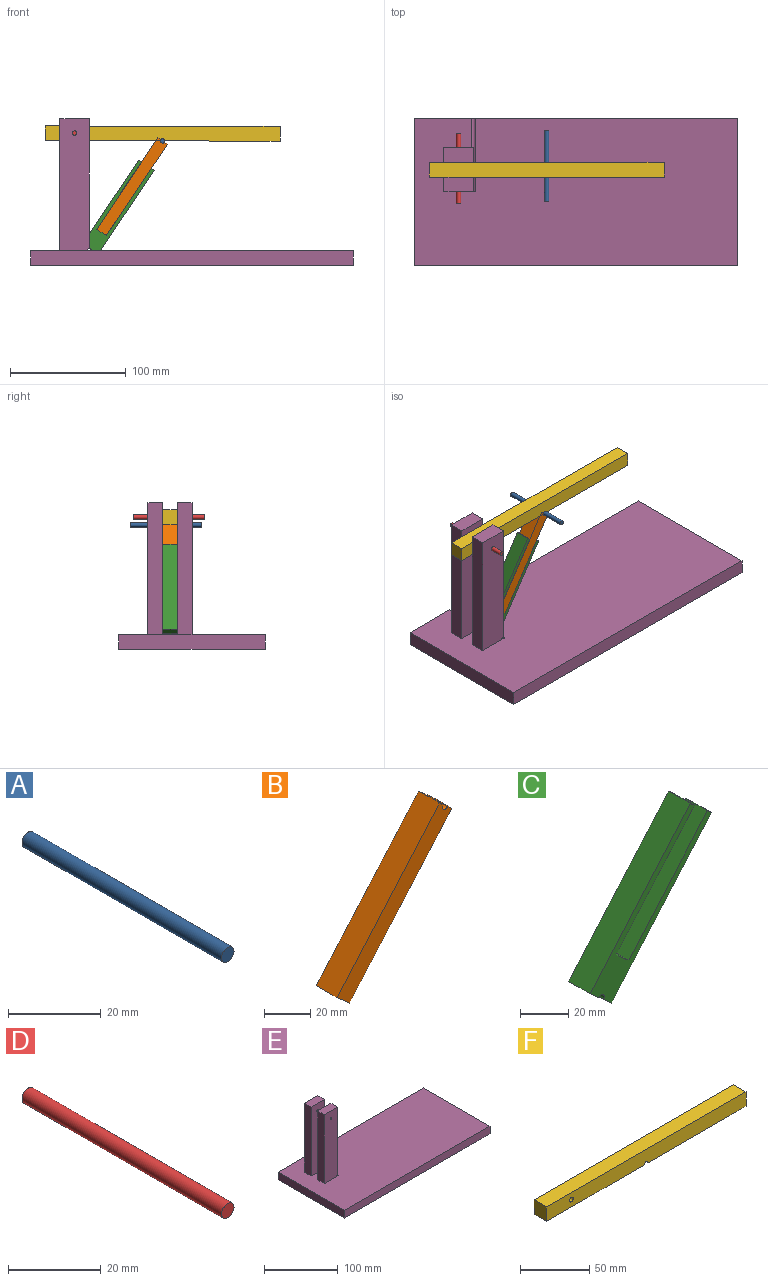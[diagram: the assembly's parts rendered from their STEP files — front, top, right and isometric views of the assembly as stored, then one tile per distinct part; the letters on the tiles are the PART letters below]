
ASSEMBLY  parts=6 mates=10
PART A: 3 faces, bbox 3.8x61x3.8 mm
  f0: cylinder r=1.91mm len=60.96mm, axis (0,1,0), area 729.7mm2, adj f1,f2
  f1: plane 3.81x3.81mm, normal (0,-1,0), area 11.4mm2, adj f0
  f2: plane 3.81x3.81mm, normal (0,1,0), area 11.4mm2, adj f0
PART B: 8 faces, bbox 70x12.7x78.4 mm
  f0: plane 12.7x2.32mm, normal (0.66,0,0.75), area 39.1mm2, adj f1,f5,f6,f7
  f1: plane 71.87x62.51mm, normal (0.75,0,-0.66), area 1209.7mm2, adj f0,f2,f5,f6
  f2: plane 12.7x7.52mm, normal (-0.66,0,-0.75), area 126.5mm2, adj f1,f3,f5,f6
  f3: plane 71.87x62.51mm, normal (-0.75,0,0.66), area 1209.7mm2, adj f2,f4,f5,f6
  f4: plane 12.7x2.32mm, normal (0.66,0,0.75), area 39.1mm2, adj f3,f5,f6,f7
  f5: plane 78.41x70.03mm, normal (0,-1,0), area 943.1mm2, adj f0,f1,f2,f3,f4,f7
  f6: plane 78.41x70.03mm, normal (0,1,0), area 943.1mm2, adj f0,f1,f2,f3,f4,f7
  f7: cylinder r=1.91mm len=12.7mm, axis (0,-1,0), area 76mm2, adj f0,f4,f5,f6
PART C: 12 faces, bbox 70.7x12.7x77.8 mm
  f0: plane 12.7x4.73mm, normal (-0.66,0,-0.75), area 79.6mm2, adj f1,f6,f7,f11
  f1: plane 77.81x70.68mm, normal (0,-1,0), area 752.1mm2, adj f0,f2,f3,f4,f5,f6,f8,f9
  f2: plane 52.7x45.84mm, normal (-0.75,0,0.66), area 887.1mm2, adj f1,f3,f7,f8
  f3: plane 12.7x2.41mm, normal (0.66,0,0.75), area 40.6mm2, adj f1,f2,f4,f7
  f4: plane 67.08x58.34mm, normal (0.75,0,-0.66), area 1129mm2, adj f1,f3,f5,f7
  f5: plane 12.7x4.73mm, normal (-0.66,0,-0.75), area 79.6mm2, adj f1,f4,f7,f11
  f6: plane 67.08x58.34mm, normal (-0.75,0,0.66), area 1129mm2, adj f0,f1,f7,f9
  f7: plane 77.81x70.68mm, normal (0,1,0), area 752.1mm2, adj f0,f2,f3,f4,f5,f6,f8,f9
  f8: plane 12.7x7.52mm, normal (0.66,0,0.75), area 126.5mm2, adj f1,f2,f7,f10
  f9: plane 12.7x2.41mm, normal (0.66,0,0.75), area 40.6mm2, adj f1,f6,f7,f10
  f10: plane 52.7x45.84mm, normal (0.75,0,-0.66), area 887.1mm2, adj f1,f7,f8,f9
  f11: cylinder r=1.91mm len=12.7mm, axis (0,-1,0), area 76mm2, adj f0,f1,f5,f7
PART D: 3 faces, bbox 3.8x61x3.8 mm
  f0: cylinder r=1.91mm len=60.96mm, axis (0,1,0), area 729.7mm2, adj f1,f2
  f1: plane 3.81x3.81mm, normal (0,-1,0), area 11.4mm2, adj f0
  f2: plane 3.81x3.81mm, normal (0,1,0), area 11.4mm2, adj f0
PART E: 20 faces, bbox 279.4x127x127 mm
  f0: plane 279.4x127mm, normal (0,0,1), area 34645.1mm2, adj f1,f2,f3,f4,f6,f8,f9,f12
  f1: plane 127x12.7mm, normal (-1,0,0), area 1612.9mm2, adj f0,f2,f4,f5
  f2: plane 279.4x12.7mm, normal (0,-1,0), area 3548.4mm2, adj f0,f1,f3,f5
  f3: plane 127x12.7mm, normal (1,0,0), area 1612.9mm2, adj f0,f2,f4,f5
  f4: plane 279.4x12.7mm, normal (0,1,0), area 3542.7mm2, adj f0,f1,f3,f5,f17
  f5: plane 279.4x127mm, normal (0,0,-1), area 35483.8mm2, adj f1,f2,f3,f4
  f6: plane 114.3x25.4mm, normal (0,-1,0), area 2889mm2, adj f0,f7,f9,f10,f17,f19
  f7: plane 112.4x12.7mm, normal (1,0,0), area 1427.4mm2, adj f6,f8,f10,f17
  f8: plane 114.3x25.4mm, normal (0,1,0), area 2889mm2, adj f0,f7,f9,f10,f17,f19
  f9: plane 114.3x12.7mm, normal (-1,0,0), area 1451.6mm2, adj f0,f6,f8,f10
  f10: plane 25.4x12.7mm, normal (0,0,1), area 322.6mm2, adj f6,f7,f8,f9
  f11: plane 112.4x12.7mm, normal (1,0,0), area 1427.4mm2, adj f12,f14,f15,f17
  f12: plane 114.3x25.4mm, normal (0,1,0), area 2889mm2, adj f0,f11,f13,f15,f16,f17
  f13: plane 114.3x12.7mm, normal (-1,0,0), area 1451.6mm2, adj f0,f12,f14,f15
  f14: plane 114.3x25.4mm, normal (0,-1,0), area 2889mm2, adj f0,f11,f13,f15,f16,f17
  f15: plane 25.4x12.7mm, normal (0,0,1), area 322.6mm2, adj f11,f12,f13,f14
  f16: cylinder r=1.91mm len=12.7mm, axis (0,-1,0), area 152mm2, adj f12,f14
  f17: cylinder r=1.91mm len=63.5mm, axis (0,-1,0), area 456mm2, adj f0,f4,f6,f7,f8,f11,f12,f14
  f18: plane 3.81x1.91mm, normal (0,1,0), area 5.7mm2, adj f0,f17
  f19: cylinder r=1.91mm len=12.7mm, axis (0,-1,0), area 152mm2, adj f6,f8
PART F: 9 faces, bbox 203.2x12.7x12.7 mm
  f0: plane 99.7x12.7mm, normal (0,0,-1), area 1266.1mm2, adj f1,f2,f3,f7
  f1: plane 203.2x12.7mm, normal (0,-1,0), area 2563.5mm2, adj f0,f2,f4,f5,f6,f7,f8
  f2: plane 12.7x12.7mm, normal (-1,0,0), area 161.3mm2, adj f0,f1,f3,f5
  f3: plane 203.2x12.7mm, normal (0,1,0), area 2563.5mm2, adj f0,f2,f4,f5,f6,f7,f8
  f4: plane 99.7x12.7mm, normal (0,0,-1), area 1266.1mm2, adj f1,f3,f6,f7
  f5: plane 203.2x12.7mm, normal (0,0,1), area 2580.6mm2, adj f1,f2,f3,f6
  f6: plane 12.7x12.7mm, normal (1,0,0), area 161.3mm2, adj f1,f3,f4,f5
  f7: cylinder r=1.91mm len=12.7mm, axis (0,-1,0), area 76mm2, adj f0,f1,f3,f4
  f8: cylinder r=1.91mm len=12.7mm, axis (0,-1,0), area 152mm2, adj f1,f3
PLACE A rot(axis=(0,-1,0),65.1deg) t=(21.12,5.24,170.36)mm
PLACE B rot(axis=(0,-1,0),7.3deg) t=(-1.49,0.55,-1.34)mm
PLACE C rot(axis=(0,-1,0),7.3deg) t=(-1.49,0.55,-1.34)mm
PLACE D rot(axis=(0,1,0),1.4deg) t=(-5.26,2.69,-15.19)mm
PLACE E t=(-2.39,0.55,-12.7)mm
PLACE F rot(axis=(0,1,0),0.2deg) t=(-2.69,0.55,-12.97)mm
MATE parallel C.f8 <-> B.f2  axis (0.56,0,0.83) through (-80.71,19.6,15.84)mm
MATE planar B.f5 <-> C.f1  axis (0,-1,0) through (-80.71,13.25,15.84)mm
MATE planar F.f1 <-> B.f5  axis (0,-1,0) through (-27.45,13.25,101.41)mm
MATE cylindrical C.f11 <-> E.f17  axis (0,-1,0) through (-91.29,13.25,0)mm
MATE cylindrical A.f0 <-> F.f7  axis (0,1,0) through (-27.8,23.02,95.05)mm
MATE planar F.f1 <-> E.f12  axis (0,-1,0) through (-27.45,13.25,101.41)mm
MATE cylindrical D.f0 <-> E.f16  axis (0,-1,0) through (-103.99,-10.01,101.78)mm
MATE cylindrical D.f0 <-> F.f8  axis (0,-1,0) through (-103.99,-10.01,101.78)mm
MATE planar B.f1 <-> C.f2  axis (0.83,0,-0.56) through (-50.11,19.6,52.68)mm
MATE cylindrical A.f0 <-> B.f7  axis (0,1,0) through (-27.8,23.02,95.05)mm
